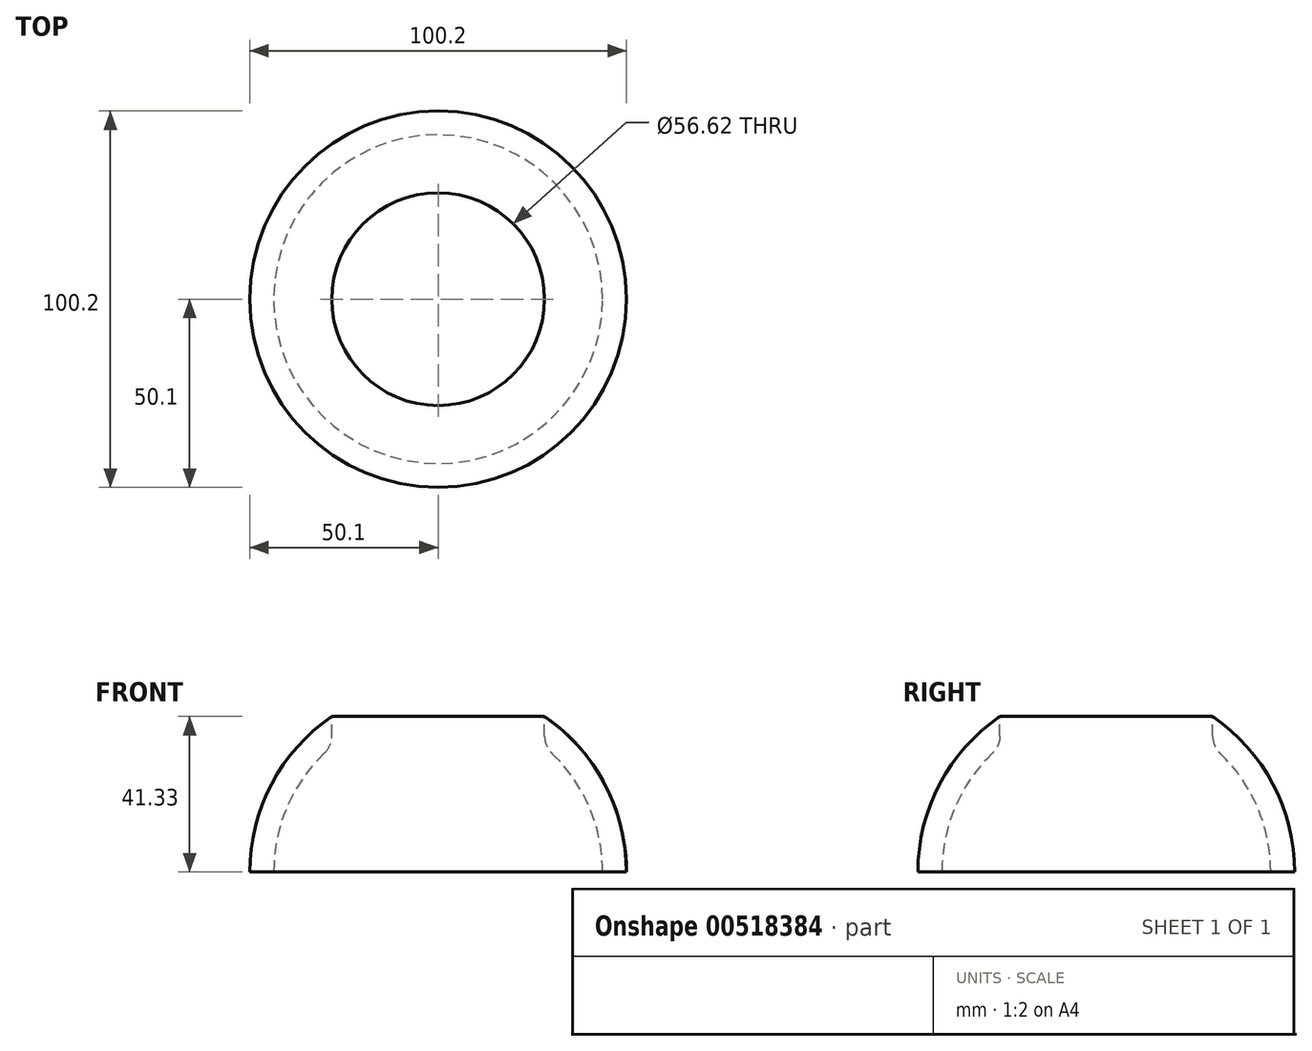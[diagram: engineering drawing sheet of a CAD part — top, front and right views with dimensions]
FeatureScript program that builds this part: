
annotation { "Feature Type Name" : "Feature", "Feature Type Description" : "" }
export const myFeature = defineFeature(function(context is Context, id is Id, definition is map)
    precondition{}
    {
        {
            var Q0;
            Q0=qCreatedBy(makeId("Front.planeOp"),FACE);
            var sketch = newSketch(context, id + "F0", { "sketchPlane" : qUnion([Q0])});
            skArc(sketch, "E0", {"start": v(0, 50.1) * mm, "mid": v(-35.43, 35.43) * mm, "end": v(-50.1, 0) * mm});
            skLineSegment(sketch, "E1", {"start": v(0, 50.1) * mm, "end": v(0, 0) * mm});
            skLineSegment(sketch, "E2", {"start": v(0, 0) * mm, "end": v(-50.1, 0) * mm});
            skLineSegment(sketch, "E3", {"start": v(0, 50.1) * mm, "end": v(0, -29.79) * mm});
            skPoint(sketch, "E3.endSnap0", {"position": v(0, 25.05) * mm});
            skSolve(sketch);
        }
        {
            var Q0;
            {var subQ0=sQuery(id+"F0.wireOp",EDGE,"E0");Q0=makeQuery(id+"F0.imprint","IMPRINT",FACE,{"disambiguationData":[TD([[makeQuery(id+"F0.imprint","IMPRINT",EDGE,{"derivedFrom":subQ0}),1.0]])]});}
            var Q1;
            Q1=sQuery(id+"F0.wireOp",EDGE,"E3");
            revolve(context, id + "F1", {"entities" : qUnion([Q0]), "axis" : qUnion([Q1]), "revolveType" : RevolveType.FULL});
        }
        {
            var Q0;
            Q0=makeQuery(id+"F1.opRevolve","SWEPT_FACE",FACE,{"disambiguationData":[OSD([sQuery(id+"F0.wireOp",EDGE,"E2")])]});
            shell(context, id + "F2", {"entities" : qUnion([Q0]), "thickness" : 6.35 * mm});
        }
        {
            var Q0;
            Q0=qCreatedBy(makeId("Top.planeOp"),FACE);
            cPlane(context, id + "F3", {"entities" : qUnion([Q0]), "cplaneType" : CPlaneType.OFFSET, "offset" : 41.27 * mm, "width" : 152.4 * mm, "height" : 152.4 * mm});
        }
        {
            var Q0;
            Q0=qCreatedBy(id+"F3.planeOp",FACE);
            var sketch = newSketch(context, id + "F4", { "sketchPlane" : qUnion([Q0])});
            skCircle(sketch, "E4", {"center": v(0, 0) * mm, "radius": 28.3 * mm});
            skSolve(sketch);
        }
        {
            var Q0;
            Q0 = qSketchRegion(id + "F4", true);
            extrude(context, id + "F5", {"entities" : qUnion([Q0]), "operationType" : NewBodyOperationType.REMOVE, "endBound" : BoundingType.SYMMETRIC, "oppositeDirection" : true, "depth" : 76.2 * mm, "offsetDistance" : 25.4 * mm});
        }
        {
            var Q0;
            Q0=makeQuery(id+"F5.boolean.opBoolean","INTERSECT",EDGE,{"derivedFrom":[makeQuery(id+"F2.opShell","OFFSET_FACE",FACE,{"disambiguationData":[OSD([sQuery(id+"F0.wireOp",EDGE,"E0")])]}),makeQuery(id+"F5.opExtrude","SWEPT_FACE",FACE,{"disambiguationData":[OSD([sQuery(id+"F4.wireOp",EDGE,"E4")])]})]});
            fillet(context, id + "F6", {"entities" : qUnion([Q0]), "radius" : 6.35 * mm, "tangentPropagation" : true, "allowEdgeOverflow" : false});
        }
    });
